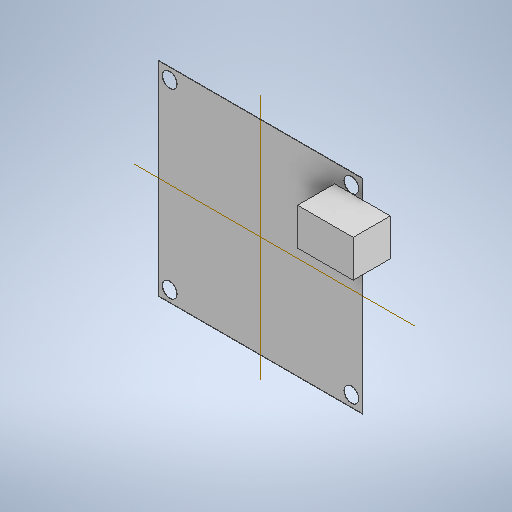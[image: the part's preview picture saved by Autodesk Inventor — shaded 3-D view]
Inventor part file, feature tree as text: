
AUTODESK INVENTOR PART (.ipt)
format: ipt  version: 2025 (Build 290162000, 162)  size: 265,216 bytes
history: native  units: in
note: dims shown in document units (in); Inventor stores cm internally (conversion verified against a paired STEP export)
features: extrude x3, sketch x3, other x1
ambient origin geometry x8: Origin, YZ Plane, XZ Plane, XY Plane, X Axis, Y Axis, Z Axis, Center Point
bodies: Body1 (feature_tree)
feature tree (7):
  other  "솔리드1"
  extrude  "돌출1"  Depth=2.1654in
  extrude  "돌출2"  Depth=2.1654in
  extrude  "돌출3"  Depth=0.0039in TaperAngle=0.0deg
  sketch  "스케치2"
  sketch  "스케치3"
  sketch  "스케치4"
